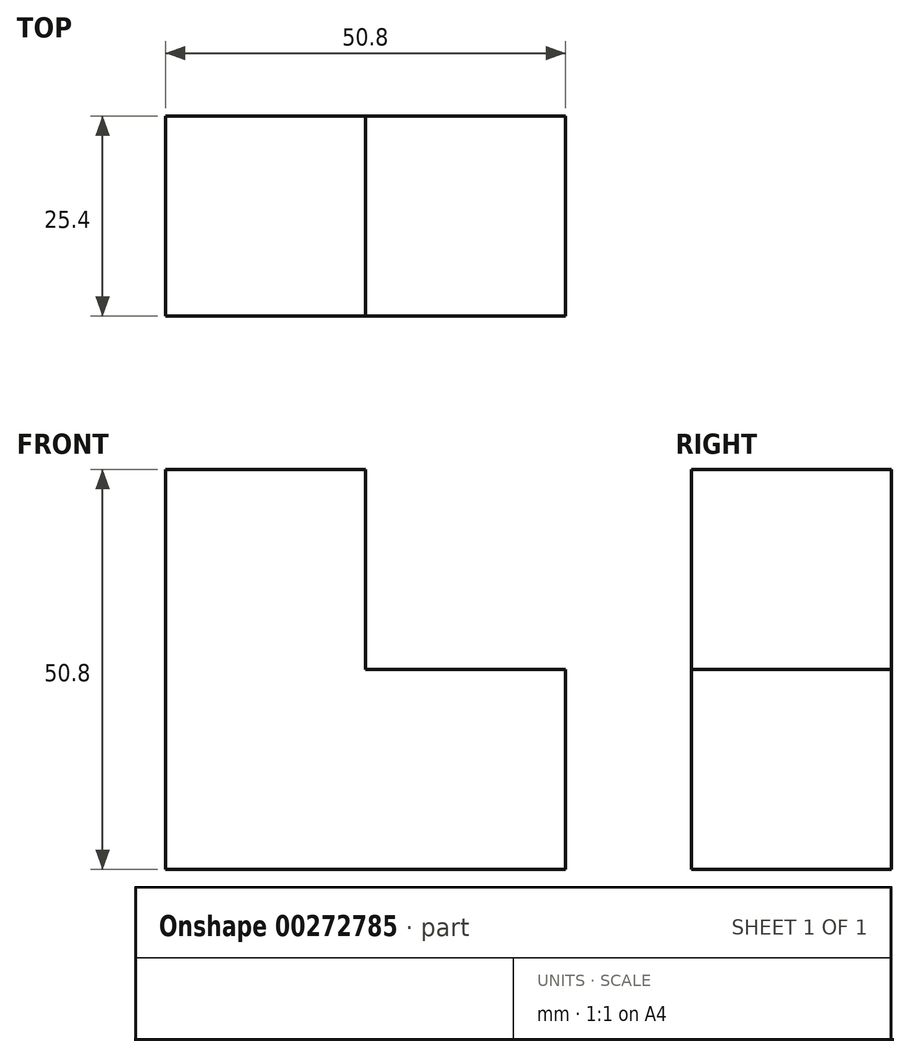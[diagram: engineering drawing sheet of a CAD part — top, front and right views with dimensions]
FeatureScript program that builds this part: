
annotation { "Feature Type Name" : "Feature", "Feature Type Description" : "" }
export const myFeature = defineFeature(function(context is Context, id is Id, definition is map)
    precondition{}
    {
        {
            var Q0;
            Q0=qCreatedBy(makeId("Front.planeOp"),FACE);
            var sketch = newSketch(context, id + "F0", { "sketchPlane" : qUnion([Q0])});
            skLineSegment(sketch, "E0", {"start": v(0, 0) * mm, "end": v(-50.8, 0) * mm});
            skLineSegment(sketch, "E1", {"start": v(-50.8, 50.8) * mm, "end": v(-25.4, 50.8) * mm});
            skLineSegment(sketch, "E2", {"start": v(-25.4, 50.8) * mm, "end": v(-25.4, 25.4) * mm});
            skLineSegment(sketch, "E3", {"start": v(-50.8, 50.8) * mm, "end": v(-50.8, 0) * mm});
            skLineSegment(sketch, "E4", {"start": v(-25.4, 25.4) * mm, "end": v(0, 25.4) * mm});
            skLineSegment(sketch, "E5", {"start": v(0, 25.4) * mm, "end": v(0, 0) * mm});
            skSolve(sketch);
        }
        {
            var Q0;
            Q0=makeQuery(id+"F0.imprint","IMPRINT",FACE,{"disambiguationData":[TD([[makeQuery(id+"F0.imprint","IMPRINT",EDGE,{"derivedFrom":sQuery(id+"F0.wireOp",EDGE,"E0")}),-1.0]])]});
            extrude(context, id + "F1", {"entities" : qUnion([Q0]), "depth" : 25.4 * mm});
        }
    });
